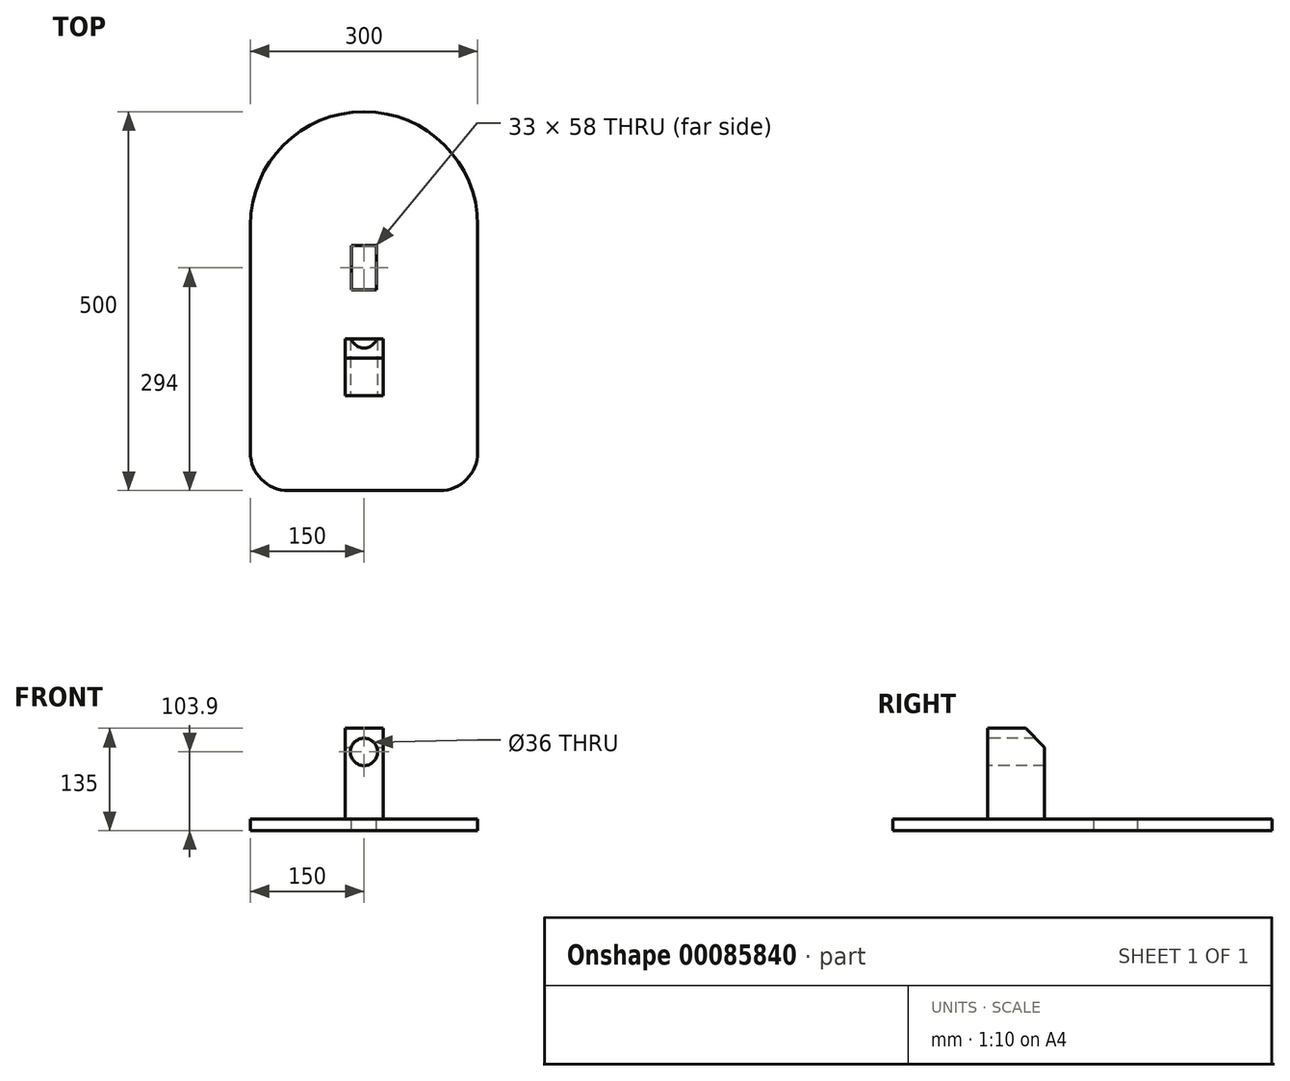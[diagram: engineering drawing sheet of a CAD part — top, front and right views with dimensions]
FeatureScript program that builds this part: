
annotation { "Feature Type Name" : "Feature", "Feature Type Description" : "" }
export const myFeature = defineFeature(function(context is Context, id is Id, definition is map)
    precondition{}
    {
        {
            var Q0;
            Q0=qCreatedBy(makeId("Top.planeOp"),FACE);
            var sketch = newSketch(context, id + "F0", { "sketchPlane" : qUnion([Q0])});
            skLineSegment(sketch, "E0.rect.bottom", {"start": v(100, -250) * mm, "end": v(-100, -250) * mm});
            skLineSegment(sketch, "E0.rect.left", {"start": v(150, -200) * mm, "end": v(150, 100) * mm});
            skLineSegment(sketch, "E0.rect.right", {"start": v(-150, -250) * mm, "end": v(-150, 100) * mm});
            skPoint(sketch, "E0.rect.middle", {"position": v(0, 0) * mm});
            skPoint(sketch, "E1.orphan", {"position": v(-150, 250) * mm});
            skPoint(sketch, "E2.orphan", {"position": v(150, 250) * mm});
            skArc(sketch, "E3", {"start": v(150, 100) * mm, "mid": v(0, 250) * mm, "end": v(-150, 100) * mm});
            skPoint(sketch, "E4.start.orphan", {"position": v(0, 250) * mm});
            skPoint(sketch, "E5.start.orphan", {"position": v(-100, 250) * mm});
            skPoint(sketch, "E6.end.orphan", {"position": v(100, 250) * mm});
            skArc(sketch, "E7", {"start": v(-150, -200) * mm, "mid": v(-135.36, -235.36) * mm, "end": v(-100, -250) * mm});
            skArc(sketch, "E8", {"start": v(100, -250) * mm, "mid": v(135.36, -235.36) * mm, "end": v(150, -200) * mm});
            skPoint(sketch, "E9.orphan", {"position": v(150, -250) * mm});
            skSolve(sketch);
        }
        {
            var Q0;
            Q0=qSketchRegion(id+"F0",true);
            extrude(context, id + "F1", {"entities" : qUnion([Q0]), "depth" : 15 * mm});
        }
        {
            var Q0;
            Q0=makeQuery(id+"F1.opExtrude","CAP_FACE",FACE,{"disambiguationData":[OSD([sQuery(id+"F0.wireOp",EDGE,"E0.rect.bottom"),sQuery(id+"F0.wireOp",EDGE,"E0.rect.left"),sQuery(id+"F0.wireOp",EDGE,"E0.rect.right"),sQuery(id+"F0.wireOp",EDGE,"E3"),sQuery(id+"F0.wireOp",EDGE,"E7"),sQuery(id+"F0.wireOp",EDGE,"E8")])],"isStart":false});
            var sketch = newSketch(context, id + "F2", { "sketchPlane" : qUnion([Q0])});
            skLineSegment(sketch, "E10.bottom", {"start": v(-16.5, 73) * mm, "end": v(16.5, 73) * mm});
            skLineSegment(sketch, "E10.top", {"start": v(-16.5, 15) * mm, "end": v(16.5, 15) * mm});
            skLineSegment(sketch, "E10.left", {"start": v(-16.5, 73) * mm, "end": v(-16.5, 15) * mm});
            skLineSegment(sketch, "E10.right", {"start": v(16.5, 73) * mm, "end": v(16.5, 15) * mm});
            skLineSegment(sketch, "E11", {"start": v(150, 100) * mm, "end": v(-52.78, 100) * mm});
            skSolve(sketch);
        }
        {
            var Q0;
            Q0=qSketchRegion(id+"F2",true);
            extrude(context, id + "F3", {"entities" : qUnion([Q0]), "operationType" : NewBodyOperationType.REMOVE, "endBound" : BoundingType.THROUGH_ALL, "oppositeDirection" : true, "depth" : 25 * mm});
        }
        {
            var Q0;
            Q0=makeQuery(id+"F1.opExtrude","CAP_FACE",FACE,{"disambiguationData":[OSD([sQuery(id+"F0.wireOp",EDGE,"E0.rect.bottom"),sQuery(id+"F0.wireOp",EDGE,"E0.rect.left"),sQuery(id+"F0.wireOp",EDGE,"E0.rect.right"),sQuery(id+"F0.wireOp",EDGE,"E3"),sQuery(id+"F0.wireOp",EDGE,"E7"),sQuery(id+"F0.wireOp",EDGE,"E8")])],"isStart":false});
            var sketch = newSketch(context, id + "F4", { "sketchPlane" : qUnion([Q0])});
            skLineSegment(sketch, "E12.bottom", {"start": v(-25, -125) * mm, "end": v(25, -125) * mm});
            skLineSegment(sketch, "E12.top", {"start": v(-25, -50) * mm, "end": v(25, -50) * mm});
            skLineSegment(sketch, "E12.left", {"start": v(-25, -125) * mm, "end": v(-25, -50) * mm});
            skLineSegment(sketch, "E12.right", {"start": v(25, -125) * mm, "end": v(25, -50) * mm});
            skPoint(sketch, "E12.middle", {"position": v(0, -87.5) * mm});
            skSolve(sketch);
        }
        {
            var Q0;
            Q0=qSketchRegion(id+"F4",true);
            extrude(context, id + "F5", {"entities" : qUnion([Q0]), "operationType" : NewBodyOperationType.ADD, "depth" : 120 * mm});
        }
        {
            var Q0;
            Q0=makeQuery(id+"F5.opExtrude","SWEPT_FACE",FACE,{"disambiguationData":[OSD([sQuery(id+"F4.wireOp",EDGE,"E12.bottom")])]});
            var sketch = newSketch(context, id + "F6", { "sketchPlane" : qUnion([Q0])});
            skCircle(sketch, "E13", {"center": v(0, 103.9) * mm, "radius": 18 * mm});
            skSolve(sketch);
        }
        {
            var Q0;
            Q0 = qSketchRegion(id + "F6", true);
            var Q1;
            Q1=makeQuery(id+"F5.opExtrude","SWEPT_FACE",FACE,{"disambiguationData":[OSD([sQuery(id+"F4.wireOp",EDGE,"E12.top")])]});
            extrude(context, id + "F7", {"entities" : qUnion([Q0]), "operationType" : NewBodyOperationType.REMOVE, "endBound" : BoundingType.UP_TO_SURFACE, "oppositeDirection" : true, "endBoundEntityFace" : qUnion([Q1]), "depth" : 25 * mm});
        }
        {
            var Q0;
            Q0=makeQuery(id+"F5.opExtrude","CAP_EDGE",EDGE,{"disambiguationData":[OSD([sQuery(id+"F4.wireOp",EDGE,"E12.top")])],"isStart":false});
            chamfer(context, id + "F8", {"entities" : qUnion([Q0]), "width" : 25 * mm, "tangentPropagation" : true});
        }
    });
